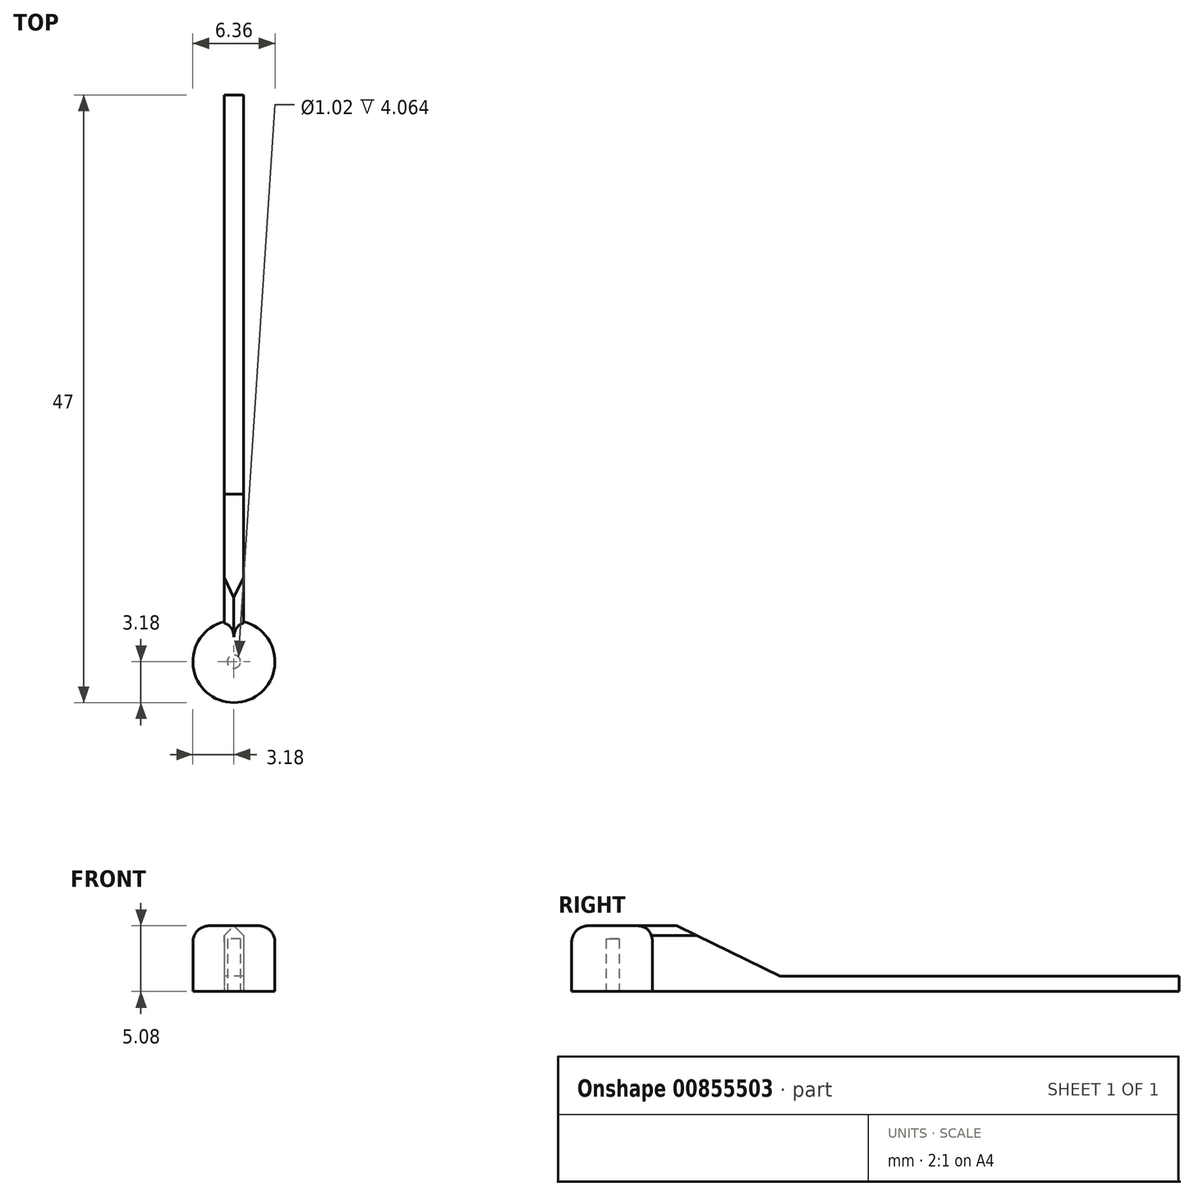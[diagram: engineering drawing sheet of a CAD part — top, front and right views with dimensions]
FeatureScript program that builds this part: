
annotation { "Feature Type Name" : "Feature", "Feature Type Description" : "" }
export const myFeature = defineFeature(function(context is Context, id is Id, definition is map)
    precondition{}
    {
        {
            var Q0;
            Q0=qCreatedBy(makeId("Top.planeOp"),FACE);
            var sketch = newSketch(context, id + "F0", { "sketchPlane" : qUnion([Q0])});
            skLineSegment(sketch, "E0", {"start": v(0, 0) * mm, "end": v(-0.76, 0) * mm});
            skLineSegment(sketch, "E1", {"start": v(0, 0) * mm, "end": v(0.76, 0) * mm});
            skCircle(sketch, "E2", {"center": v(0, 0) * mm, "radius": 3.18 * mm});
            skLineSegment(sketch, "E3", {"start": v(-0.76, 0) * mm, "end": v(-0.76, 43.82) * mm});
            skLineSegment(sketch, "E4", {"start": v(0.76, 0) * mm, "end": v(0.76, 43.81) * mm});
            skLineSegment(sketch, "E5", {"start": v(0.76, 43.81) * mm, "end": v(-0.76, 43.82) * mm});
            skSolve(sketch);
        }
        {
            var Q0;
            Q0=qSketchRegion(id+"F0",true);
            var Q1;
            {var subQ0=sQuery(id+"F0.wireOp",EDGE,"E1");var subQ1=sQuery(id+"F0.wireOp",EDGE,"E0");var subQ2=makeQuery(id+"F0.imprint","INTERSECT",VERTEX,{"derivedFrom":[subQ1,subQ0]});Q1=makeQuery(id+"F0.imprint","IMPRINT",FACE,{"disambiguationData":[TD([[makeQuery(id+"F0.imprint","IMPRINT",EDGE,{"disambiguationData":[TD([[subQ2,-1.0]])],"derivedFrom":subQ1}),-1.0]])]});}
            var Q2;
            {var subQ0=sQuery(id+"F0.wireOp",EDGE,"E1");var subQ1=sQuery(id+"F0.wireOp",EDGE,"E0");var subQ2=makeQuery(id+"F0.imprint","INTERSECT",VERTEX,{"derivedFrom":[subQ1,subQ0]});Q2=makeQuery(id+"F0.imprint","IMPRINT",FACE,{"disambiguationData":[TD([[makeQuery(id+"F0.imprint","IMPRINT",EDGE,{"disambiguationData":[TD([[subQ2,-1.0]])],"derivedFrom":subQ1}),1.0]])]});}
            extrude(context, id + "F1", {"entities" : qUnion([Q0, Q1, Q2]), "depth" : 5.08 * mm, "offsetDistance" : 25.4 * mm});
        }
        {
            var Q0;
            Q0=makeQuery(id+"F1.opExtrude","CAP_EDGE",EDGE,{"disambiguationData":[OSD([sQuery(id+"F0.wireOp",EDGE,"E3")])],"isStart":false});
            var Q1;
            Q1=makeQuery(id+"F1.opExtrude","CAP_EDGE",EDGE,{"disambiguationData":[OSD([sQuery(id+"F0.wireOp",EDGE,"E4")])],"isStart":false});
            chamfer(context, id + "F2", {"entities" : qUnion([Q0, Q1]), "width" : 0.76 * mm, "tangentPropagation" : true});
        }
        {
            var Q0;
            Q0=makeQuery(id+"F1.opExtrude","CAP_EDGE",EDGE,{"disambiguationData":[OSD([sQuery(id+"F0.wireOp",EDGE,"E2")])],"isStart":false});
            fillet(context, id + "F3", {"entities" : qUnion([Q0]), "radius" : 1.27 * mm, "tangentPropagation" : true, "allowEdgeOverflow" : false});
        }
        {
            var Q0;
            Q0=qCreatedBy(makeId("Top.planeOp"),FACE);
            var sketch = newSketch(context, id + "F4", { "sketchPlane" : qUnion([Q0])});
            skCircle(sketch, "E6", {"center": v(0, 0) * mm, "radius": 0.5 * mm});
            skSolve(sketch);
        }
        {
            var Q0;
            Q0=qSketchRegion(id+"F4",true);
            extrude(context, id + "F5", {"entities" : qUnion([Q0]), "operationType" : NewBodyOperationType.REMOVE, "depth" : 4.06 * mm, "offsetDistance" : 25.4 * mm});
        }
        {
            var Q0;
            Q0=qCreatedBy(makeId("Right.planeOp"),FACE);
            var sketch = newSketch(context, id + "F6", { "sketchPlane" : qUnion([Q0])});
            skLineSegment(sketch, "E7", {"start": v(-3.41, 9.15) * mm, "end": v(12.95, 1.18) * mm});
            skLineSegment(sketch, "E8", {"start": v(12.95, 1.18) * mm, "end": v(47.1, 1.18) * mm});
            skLineSegment(sketch, "E9", {"start": v(47.1, 1.18) * mm, "end": v(47.1, 6.88) * mm});
            skLineSegment(sketch, "E10", {"start": v(47.1, 6.88) * mm, "end": v(-3.41, 9.15) * mm});
            skSolve(sketch);
        }
        {
            var Q0;
            Q0 = qSketchRegion(id + "F6", true);
            extrude(context, id + "F7", {"entities" : qUnion([Q0]), "operationType" : NewBodyOperationType.REMOVE, "depth" : 5.08 * mm, "offsetDistance" : 25.4 * mm, "hasSecondDirection" : true, "secondDirectionOppositeDirection" : true, "secondDirectionDepth" : 5.08 * mm});
        }
    });
